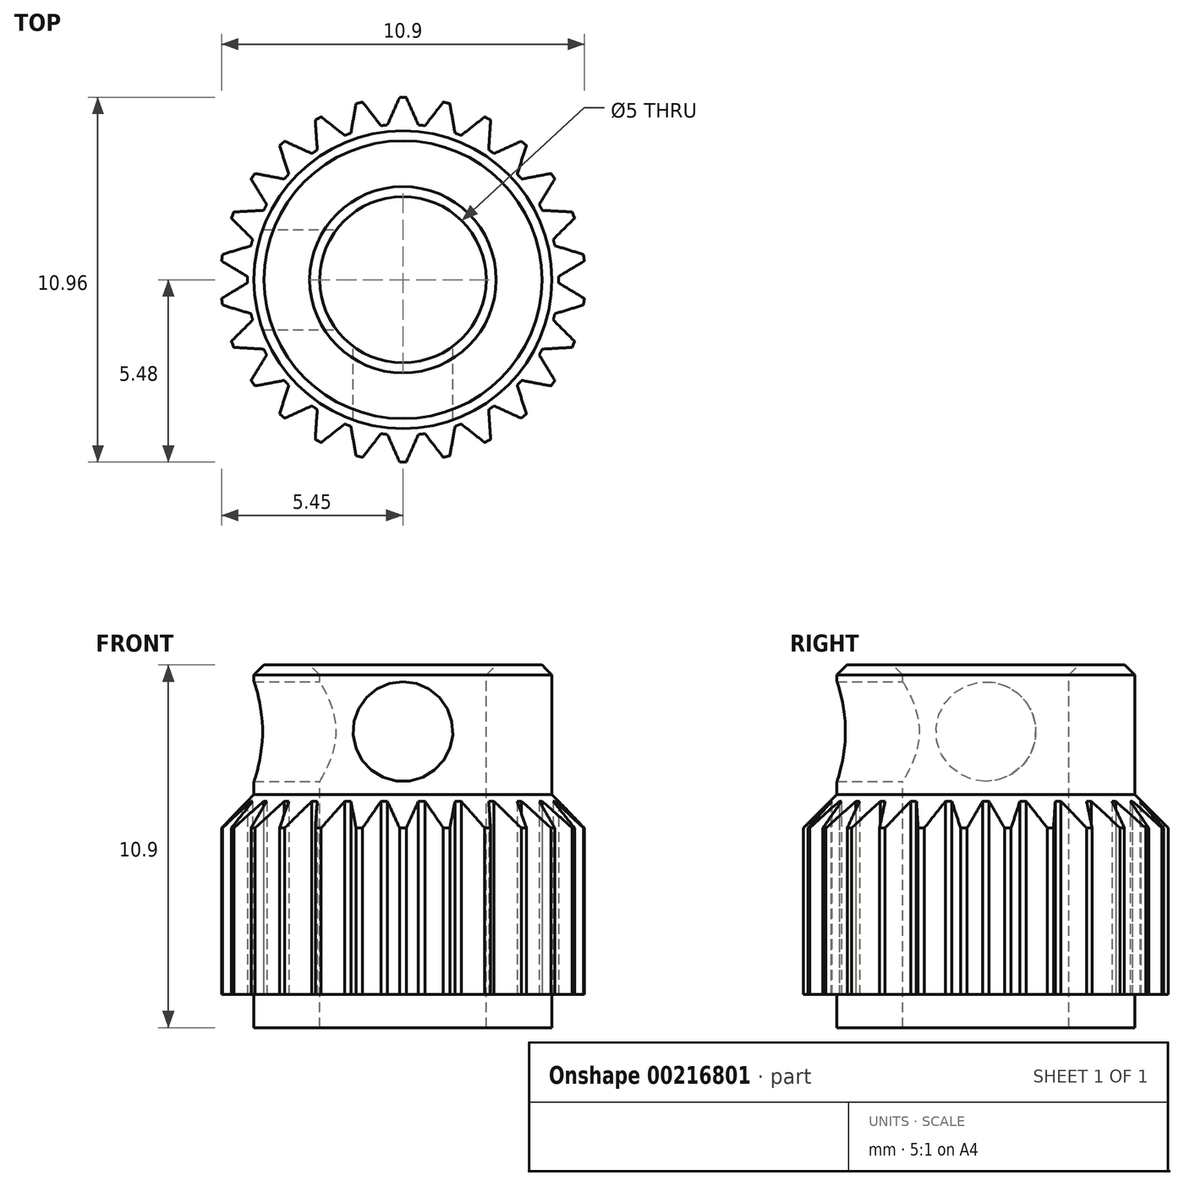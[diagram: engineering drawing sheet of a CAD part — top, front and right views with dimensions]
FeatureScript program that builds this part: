
annotation { "Feature Type Name" : "Feature", "Feature Type Description" : "" }
export const myFeature = defineFeature(function(context is Context, id is Id, definition is map)
    precondition{}
    {
        {
            var Q0;
            Q0=qCreatedBy(makeId("Top.planeOp"),FACE);
            var sketch = newSketch(context, id + "F0", { "sketchPlane" : qUnion([Q0])});
            skCircle(sketch, "E0", {"center": v(0, 0) * mm, "radius": 5.47 * mm});
            skCircle(sketch, "E1", {"center": v(0, 0) * mm, "radius": 4.47 * mm});
            skCircle(sketch, "E2.0", {"center": v(0, 0) * mm, "radius": 4.67 * mm});
            skSolve(sketch);
        }
        {
            var Q0;
            Q0=qCreatedBy(makeId("Top.planeOp"),FACE);
            var sketch = newSketch(context, id + "F1", { "sketchPlane" : qUnion([Q0])});
            skLineSegment(sketch, "E3", {"start": v(-0.5, 4.58) * mm, "end": v(0.5, 4.58) * mm});
            skPoint(sketch, "E4", {"position": v(0, 4.58) * mm});
            skLineSegment(sketch, "E5", {"start": v(-0.5, 4.58) * mm, "end": v(-0.1, 5.47) * mm});
            skLineSegment(sketch, "E6", {"start": v(-0.1, 5.47) * mm, "end": v(0.1, 5.47) * mm});
            skLineSegment(sketch, "E7", {"start": v(0.1, 5.47) * mm, "end": v(0.5, 4.58) * mm});
            skPoint(sketch, "E8", {"position": v(0, 5.47) * mm});
            skSolve(sketch);
        }
        {
            var Q0;
            Q0=makeQuery(id+"F1.imprint","IMPRINT",FACE,{"disambiguationData":[TD([[makeQuery(id+"F1.imprint","IMPRINT",EDGE,{"derivedFrom":sQuery(id+"F1.wireOp",EDGE,"E3")}),1.0]])]});
            extrude(context, id + "F2", {"entities" : qUnion([Q0]), "depth" : 5 * mm});
        }
        {
            var Q0;
            Q0=makeQuery(id+"F2.opExtrude","SWEPT_BODY",BODY,{"disambiguationData":[OSD([sQuery(id+"F1.wireOp",EDGE,"E3"),sQuery(id+"F1.wireOp",EDGE,"E5"),sQuery(id+"F1.wireOp",EDGE,"E6"),sQuery(id+"F1.wireOp",EDGE,"E7")])]});
            var Q1;
            Q1=sQuery(id+"F0.wireOp",EDGE,"E0");
            circularPattern(context, id + "F3", {"entities" : qUnion([Q0]), "axis" : qUnion([Q1]), "angle" : 360 * degree, "instanceCount" : 26, "equalSpace" : true});
        }
        {
            var Q0;
            Q0=makeQuery(id+"F0.imprint","IMPRINT",FACE,{"disambiguationData":[TD([[makeQuery(id+"F0.imprint","IMPRINT",EDGE,{"derivedFrom":sQuery(id+"F0.wireOp",EDGE,"E1")}),-1.0]])]});
            var Q1;
            Q1=makeQuery(id+"F0.imprint","IMPRINT",FACE,{"disambiguationData":[TD([[makeQuery(id+"F0.imprint","IMPRINT",EDGE,{"derivedFrom":sQuery(id+"F0.wireOp",EDGE,"E1")}),1.0]])]});
            extrude(context, id + "F4", {"entities" : qUnion([Q0, Q1]), "operationType" : NewBodyOperationType.ADD, "depth" : 5 * mm});
        }
        {
            var Q0;
            Q0=makeQuery(id+"F0.imprint","IMPRINT",FACE,{"disambiguationData":[TD([[makeQuery(id+"F0.imprint","IMPRINT",EDGE,{"derivedFrom":sQuery(id+"F0.wireOp",EDGE,"E1")}),1.0]])]});
            extrude(context, id + "F5", {"entities" : qUnion([Q0]), "operationType" : NewBodyOperationType.ADD, "depth" : 9.9 * mm});
        }
        {
            var Q0;
            Q0=makeQuery(id+"F0.imprint","IMPRINT",FACE,{"disambiguationData":[TD([[makeQuery(id+"F0.imprint","IMPRINT",EDGE,{"derivedFrom":sQuery(id+"F0.wireOp",EDGE,"E1")}),1.0]])]});
            extrude(context, id + "F6", {"entities" : qUnion([Q0]), "operationType" : NewBodyOperationType.ADD, "oppositeDirection" : true, "depth" : 1 * mm});
        }
        {
            var Q0;
            {var subQ0=makeQuery(id+"F2.opExtrude","CAP_FACE",FACE,{"disambiguationData":[OSD([sQuery(id+"F1.wireOp",EDGE,"E3"),sQuery(id+"F1.wireOp",EDGE,"E5"),sQuery(id+"F1.wireOp",EDGE,"E6"),sQuery(id+"F1.wireOp",EDGE,"E7")])],"isStart":false});Q0=makeQuery(id+"F5.boolean.opBoolean","INTERSECT",EDGE,{"derivedFrom":[makeQuery(id+"F4.boolean.opBoolean","MERGE",FACE,{"derivedFrom":[subQ0,makeQuery(id+"F3.opPattern","COPY",FACE,{"derivedFrom":subQ0,"instanceName":"1"}),makeQuery(id+"F3.opPattern","COPY",FACE,{"derivedFrom":subQ0,"instanceName":"2"}),makeQuery(id+"F3.opPattern","COPY",FACE,{"derivedFrom":subQ0,"instanceName":"3"}),makeQuery(id+"F3.opPattern","COPY",FACE,{"derivedFrom":subQ0,"instanceName":"4"}),makeQuery(id+"F3.opPattern","COPY",FACE,{"derivedFrom":subQ0,"instanceName":"5"}),makeQuery(id+"F3.opPattern","COPY",FACE,{"derivedFrom":subQ0,"instanceName":"6"}),makeQuery(id+"F3.opPattern","COPY",FACE,{"derivedFrom":subQ0,"instanceName":"7"}),makeQuery(id+"F3.opPattern","COPY",FACE,{"derivedFrom":subQ0,"instanceName":"8"}),makeQuery(id+"F3.opPattern","COPY",FACE,{"derivedFrom":subQ0,"instanceName":"9"}),makeQuery(id+"F3.opPattern","COPY",FACE,{"derivedFrom":subQ0,"instanceName":"10"}),makeQuery(id+"F3.opPattern","COPY",FACE,{"derivedFrom":subQ0,"instanceName":"11"}),makeQuery(id+"F3.opPattern","COPY",FACE,{"derivedFrom":subQ0,"instanceName":"12"}),makeQuery(id+"F3.opPattern","COPY",FACE,{"derivedFrom":subQ0,"instanceName":"13"}),makeQuery(id+"F3.opPattern","COPY",FACE,{"derivedFrom":subQ0,"instanceName":"14"}),makeQuery(id+"F3.opPattern","COPY",FACE,{"derivedFrom":subQ0,"instanceName":"15"}),makeQuery(id+"F3.opPattern","COPY",FACE,{"derivedFrom":subQ0,"instanceName":"16"}),makeQuery(id+"F3.opPattern","COPY",FACE,{"derivedFrom":subQ0,"instanceName":"17"}),makeQuery(id+"F3.opPattern","COPY",FACE,{"derivedFrom":subQ0,"instanceName":"18"}),makeQuery(id+"F3.opPattern","COPY",FACE,{"derivedFrom":subQ0,"instanceName":"19"}),makeQuery(id+"F3.opPattern","COPY",FACE,{"derivedFrom":subQ0,"instanceName":"20"}),makeQuery(id+"F3.opPattern","COPY",FACE,{"derivedFrom":subQ0,"instanceName":"21"}),makeQuery(id+"F3.opPattern","COPY",FACE,{"derivedFrom":subQ0,"instanceName":"22"}),makeQuery(id+"F3.opPattern","COPY",FACE,{"derivedFrom":subQ0,"instanceName":"23"}),makeQuery(id+"F3.opPattern","COPY",FACE,{"derivedFrom":subQ0,"instanceName":"24"}),makeQuery(id+"F3.opPattern","COPY",FACE,{"derivedFrom":subQ0,"instanceName":"25"}),makeQuery(id+"F4.opExtrude","CAP_FACE",FACE,{"disambiguationData":[OSD([sQuery(id+"F0.wireOp",EDGE,"E2.0")])],"isStart":false})]}),makeQuery(id+"F5.opExtrude","SWEPT_FACE",FACE,{"disambiguationData":[OSD([sQuery(id+"F0.wireOp",EDGE,"E1")])]})]});}
            var Q1;
            Q1=makeQuery(id+"F6.opExtrude","CAP_EDGE",EDGE,{"disambiguationData":[OSD([sQuery(id+"F0.wireOp",EDGE,"E1")])],"isStart":true});
            chamfer(context, id + "F7", {"entities" : qUnion([Q0, Q1]), "width" : 1 * mm, "tangentPropagation" : true});
        }
        {
            var Q0;
            Q0=makeQuery(id+"F5.opExtrude","CAP_FACE",FACE,{"disambiguationData":[OSD([sQuery(id+"F0.wireOp",EDGE,"E1")])],"isStart":false});
            var sketch = newSketch(context, id + "F8", { "sketchPlane" : qUnion([Q0])});
            skPoint(sketch, "E9", {"position": v(0, 0) * mm});
            skSolve(sketch);
        }
        {
            var Q0;
            Q0=sQuery(id+"F8.wireOp",VERTEX,"E9");
            var Q1;
            Q1=makeQuery(id+"F2.opExtrude","SWEPT_BODY",BODY,{"disambiguationData":[OSD([sQuery(id+"F1.wireOp",EDGE,"E3"),sQuery(id+"F1.wireOp",EDGE,"E5"),sQuery(id+"F1.wireOp",EDGE,"E6"),sQuery(id+"F1.wireOp",EDGE,"E7")])]});
            hole(context, id + "F9", {"style" : HoleStyle.SIMPLE, "endStyle" : HoleEndStyle.THROUGH, "holeDiameter" : 5 * mm, "locations" : qUnion([Q0]), "scope" : qUnion([Q1]), "isTappedThrough" : true});
        }
        {
            var Q0;
            Q0=makeQuery(id+"F5.opExtrude","CAP_FACE",FACE,{"disambiguationData":[OSD([sQuery(id+"F0.wireOp",EDGE,"E1")])],"isStart":false});
            var Q1;
            Q1=makeQuery(id+"F9.hole-0.boolean.opBoolean","INTERSECT",EDGE,{"derivedFrom":[makeQuery(id+"F6.opExtrude","CAP_FACE",FACE,{"disambiguationData":[OSD([sQuery(id+"F0.wireOp",EDGE,"E1")])],"isStart":false}),makeQuery(id+"F9.hole-0.opRevolve","SWEPT_FACE",FACE,{"disambiguationData":[OSD([sQuery(id+"F9.hole-0.sketch.wireOp",EDGE,"core_line_2")])]})]});
            chamfer(context, id + "F10", {"entities" : qUnion([Q0, Q1]), "width" : 0.3 * mm, "tangentPropagation" : true});
        }
        {
            var Q0;
            Q0=qCreatedBy(makeId("Front.planeOp"),FACE);
            var sketch = newSketch(context, id + "F11", { "sketchPlane" : qUnion([Q0])});
            skPoint(sketch, "E10", {"position": v(0, 7.9) * mm});
            skSolve(sketch);
        }
        {
            var Q0;
            Q0=sQuery(id+"F11.wireOp",VERTEX,"E10");
            var Q1;
            Q1=makeQuery(id+"F2.opExtrude","SWEPT_BODY",BODY,{"disambiguationData":[OSD([sQuery(id+"F1.wireOp",EDGE,"E3"),sQuery(id+"F1.wireOp",EDGE,"E5"),sQuery(id+"F1.wireOp",EDGE,"E6"),sQuery(id+"F1.wireOp",EDGE,"E7")])]});
            hole(context, id + "F12", {"style" : HoleStyle.SIMPLE, "endStyle" : HoleEndStyle.THROUGH, "oppositeDirection" : true, "holeDiameter" : 3 * mm, "locations" : qUnion([Q0]), "scope" : qUnion([Q1]), "isTappedThrough" : true});
        }
        {
            var Q0;
            Q0=qCreatedBy(makeId("Right.planeOp"),FACE);
            var sketch = newSketch(context, id + "F13", { "sketchPlane" : qUnion([Q0])});
            skPoint(sketch, "E11", {"position": v(0, 7.9) * mm});
            skSolve(sketch);
        }
        {
            var Q0;
            Q0=sQuery(id+"F13.wireOp",VERTEX,"E11");
            var Q1;
            Q1=makeQuery(id+"F2.opExtrude","SWEPT_BODY",BODY,{"disambiguationData":[OSD([sQuery(id+"F1.wireOp",EDGE,"E3"),sQuery(id+"F1.wireOp",EDGE,"E5"),sQuery(id+"F1.wireOp",EDGE,"E6"),sQuery(id+"F1.wireOp",EDGE,"E7")])]});
            hole(context, id + "F14", {"style" : HoleStyle.SIMPLE, "endStyle" : HoleEndStyle.THROUGH, "holeDiameter" : 3 * mm, "locations" : qUnion([Q0]), "scope" : qUnion([Q1]), "isTappedThrough" : true});
        }
    });
